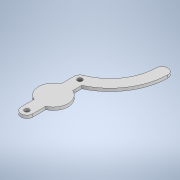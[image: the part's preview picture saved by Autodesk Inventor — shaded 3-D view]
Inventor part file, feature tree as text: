
AUTODESK INVENTOR PART (.ipt)
format: ipt  version: 2021 (Build 250183000, 183)  size: 133,120 bytes
history: native  units: mm
features: other x1, extrude x1, sketch x1
ambient origin geometry x8: Origin, YZ Plane, XZ Plane, XY Plane, X Axis, Y Axis, Z Axis, Center Point
bodies: Solid1 (feature_tree)
feature tree (3):
  other  "<userpath>\Documents\Semestre8\Robótica\Proyecto-Rob\Piezas\ParámetrosGripper.xlsx"
  extrude  "Extrusion1"  Depth=5.0mm
  sketch  "Sketch1"  dims[d0=20.0mm d2=90.0mm d3=8.0mm d4=8.0mm d5=20.0mm d7=100.0mm d8=25.307274mm d9=100.0mm d10=50.0mm d11=5.0mm d12=0.0mm]
